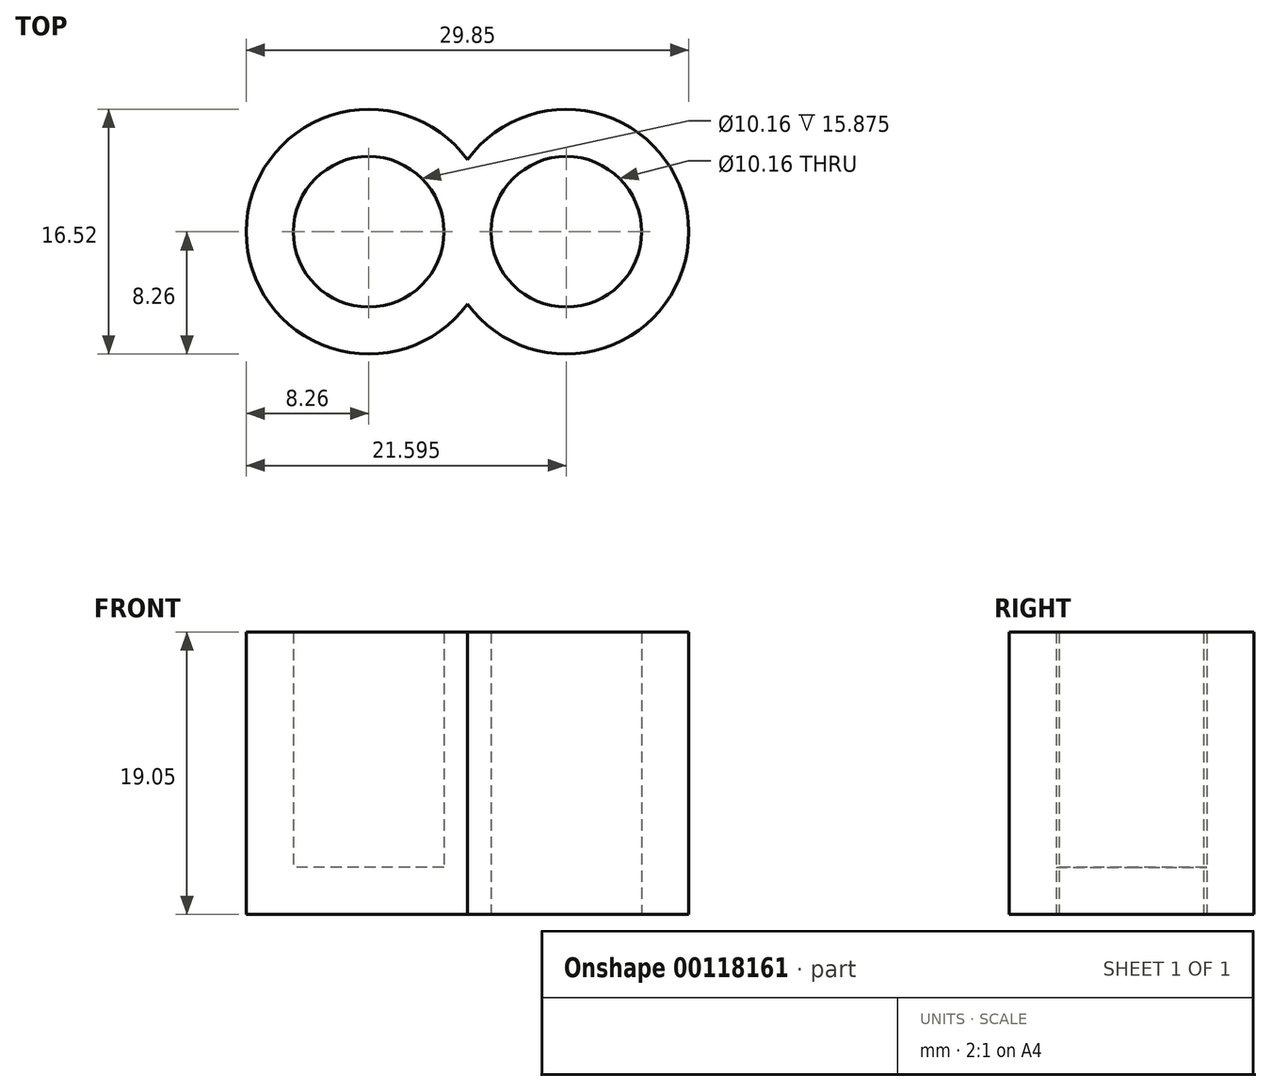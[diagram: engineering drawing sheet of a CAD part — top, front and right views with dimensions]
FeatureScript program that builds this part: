
annotation { "Feature Type Name" : "Feature", "Feature Type Description" : "" }
export const myFeature = defineFeature(function(context is Context, id is Id, definition is map)
    precondition{}
    {
        {
            var Q0;
            Q0=qCreatedBy(makeId("Top.planeOp"),FACE);
            var sketch = newSketch(context, id + "F0", { "sketchPlane" : qUnion([Q0])});
            skCircle(sketch, "E0", {"center": v(0, 0) * mm, "radius": 5.08 * mm});
            skLineSegment(sketch, "E1", {"start": v(0, 0) * mm, "end": v(8.26, 0) * mm});
            skLineSegment(sketch, "E2", {"start": v(8.26, 0) * mm, "end": v(5.08, 0) * mm});
            skLineSegment(sketch, "E3", {"start": v(5.08, 0) * mm, "end": v(13.34, 0) * mm});
            skCircle(sketch, "E4", {"center": v(13.34, 0) * mm, "radius": 5.08 * mm});
            skCircle(sketch, "E5", {"center": v(0, 0) * mm, "radius": 8.26 * mm});
            skCircle(sketch, "E6", {"center": v(13.34, 0) * mm, "radius": 8.26 * mm});
            skSolve(sketch);
        }
        {
            var Q0;
            {var subQ0=sQuery(id+"F0.wireOp",EDGE,"E0");Q0=makeQuery(id+"F0.imprint","IMPRINT",FACE,{"disambiguationData":[TD([[makeQuery(id+"F0.imprint","IMPRINT",EDGE,{"derivedFrom":subQ0}),-1.0]])]});}
            var Q1;
            {var subQ0=sQuery(id+"F0.wireOp",EDGE,"E6");var subQ3=sQuery(id+"F0.wireOp",EDGE,"E5");var subQ5=makeQuery(id+"F0.imprint","INTERSECT",VERTEX,{"disambiguationData":[OD(1.0)],"derivedFrom":[subQ3,subQ0]});Q1=makeQuery(id+"F0.imprint","IMPRINT",FACE,{"disambiguationData":[TD([[makeQuery(id+"F0.imprint","IMPRINT",EDGE,{"disambiguationData":[TD([[subQ5,-1.0]])],"derivedFrom":subQ3}),1.0]])]});}
            var Q2;
            {var subQ0=sQuery(id+"F0.wireOp",EDGE,"E6");var subQ3=sQuery(id+"F0.wireOp",EDGE,"E5");var subQ5=makeQuery(id+"F0.imprint","INTERSECT",VERTEX,{"disambiguationData":[OD(0.0)],"derivedFrom":[subQ3,subQ0]});Q2=makeQuery(id+"F0.imprint","IMPRINT",FACE,{"disambiguationData":[TD([[makeQuery(id+"F0.imprint","IMPRINT",EDGE,{"disambiguationData":[TD([[subQ5,1.0]])],"derivedFrom":subQ3}),1.0]])]});}
            var Q3;
            {var subQ0=sQuery(id+"F0.wireOp",EDGE,"E4");Q3=makeQuery(id+"F0.imprint","IMPRINT",FACE,{"disambiguationData":[TD([[makeQuery(id+"F0.imprint","IMPRINT",EDGE,{"derivedFrom":subQ0}),-1.0]])]});}
            extrude(context, id + "F1", {"entities" : qUnion([Q0, Q1, Q2, Q3]), "depth" : 19.05 * mm});
        }
        {
            var Q0;
            Q0=qCreatedBy(makeId("Top.planeOp"),FACE);
            var sketch = newSketch(context, id + "F2", { "sketchPlane" : qUnion([Q0])});
            skCircle(sketch, "E7", {"center": v(0, 0) * mm, "radius": 5.08 * mm});
            skSolve(sketch);
        }
        {
            var Q0;
            Q0=makeQuery(id+"F2.imprint","IMPRINT",FACE,{"disambiguationData":[TD([[makeQuery(id+"F2.imprint","IMPRINT",EDGE,{"derivedFrom":sQuery(id+"F2.wireOp",EDGE,"E7")}),1.0]])]});
            extrude(context, id + "F3", {"entities" : qUnion([Q0]), "operationType" : NewBodyOperationType.ADD, "depth" : 3.17 * mm});
        }
    });
